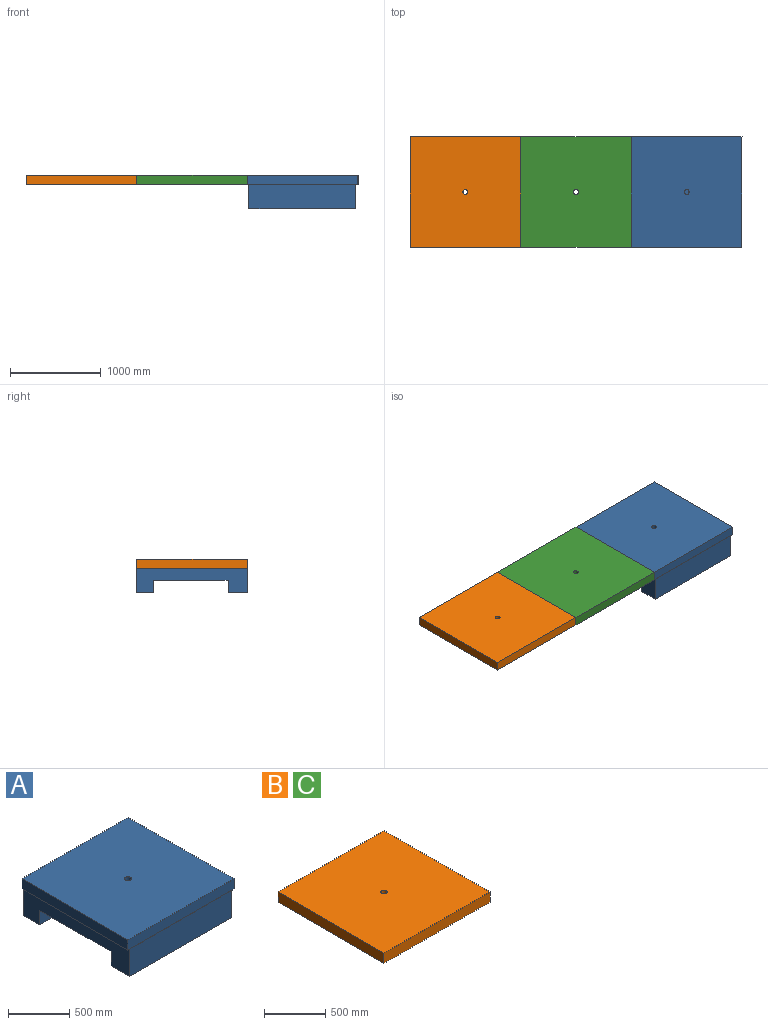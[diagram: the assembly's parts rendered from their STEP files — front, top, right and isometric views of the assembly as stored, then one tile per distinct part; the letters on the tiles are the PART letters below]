
ASSEMBLY  parts=3 mates=2
PART A: 17 faces, bbox 1219.2x1219.2x374 mm
  f0: plane 1219.2x1219.2mm, normal (0,0,-1), area 59318.6mm2, adj f1,f2,f3,f5,f7,f8,f9,f10
  f1: plane 1219.2x101.6mm, normal (0,-1,0), area 123870.7mm2, adj f0,f2,f5,f6
  f2: plane 1219.2x101.6mm, normal (1,0,0), area 123870.7mm2, adj f0,f1,f3,f6
  f3: plane 1219.2x101.6mm, normal (0,1,0), area 123870.7mm2, adj f0,f2,f5,f6
  f4: cylinder r=27.54mm len=101.6mm, axis (0,0,-1), area 17582mm2, adj f6,f16
  f5: plane 1219.2x101.6mm, normal (-1,0,0), area 123870.7mm2, adj f0,f1,f3,f6
  f6: plane 1219.2x1219.2mm, normal (0,0,1), area 1484065.6mm2, adj f1,f2,f3,f4,f5
  f7: plane 1216.15x272.36mm, normal (-1,0,0), area 214341.6mm2, adj f0,f9,f10,f11,f12,f13,f14,f15
  f8: plane 1216.15x272.36mm, normal (1,0,0), area 214341.6mm2, adj f0,f9,f10,f11,f12,f13,f14,f15
  f9: plane 1173.48x272.36mm, normal (0,-1,0), area 319607.7mm2, adj f0,f7,f8,f15
  f10: plane 1173.48x272.36mm, normal (0,1,0), area 319607.7mm2, adj f0,f7,f8,f11
  f11: plane 1173.48x187.56mm, normal (0,0,-1), area 220095.9mm2, adj f7,f8,f10,f12
  f12: plane 1173.48x142.9mm, normal (0,-1,0), area 167692.2mm2, adj f7,f8,f11,f13
  f13: plane 1173.48x817.96mm, normal (0,0,-1), area 959862.9mm2, adj f7,f8,f12,f14
  f14: plane 1173.48x142.9mm, normal (0,1,0), area 167692.2mm2, adj f7,f8,f13,f15
  f15: plane 1173.48x210.63mm, normal (0,0,-1), area 247171.2mm2, adj f7,f8,f9,f14
  f16: plane 55.08x55.08mm, normal (0,0,1), area 2383.1mm2, adj f4
PART B: 7 faces, bbox 1219.2x1219.2x101.6 mm
  f0: plane 1219.2x101.6mm, normal (0,-1,0), area 123870.7mm2, adj f1,f4,f5,f6
  f1: plane 1219.2x101.6mm, normal (1,0,0), area 123870.7mm2, adj f0,f2,f5,f6
  f2: plane 1219.2x101.6mm, normal (0,1,0), area 123870.7mm2, adj f1,f4,f5,f6
  f3: cylinder r=26.3mm len=101.6mm, axis (0,0,-1), area 16791mm2, adj f5,f6
  f4: plane 1219.2x101.6mm, normal (-1,0,0), area 123870.7mm2, adj f0,f2,f5,f6
  f5: plane 1219.2x1219.2mm, normal (0,0,1), area 1484275.2mm2, adj f0,f1,f2,f3,f4
  f6: plane 1219.2x1219.2mm, normal (0,0,-1), area 1484275.2mm2, adj f0,f1,f2,f3,f4
PART C: same geometry as B
PLACE A t=(-42.52,28.94,-4.42)mm
PLACE B t=(-2480.92,28.94,-4.42)mm
PLACE C t=(-1261.72,28.94,-4.42)mm
MATE planar C.f3 <-> A.f4  axis (0,0,1) through (-1261.72,28.94,97.18)mm
MATE planar B.f3 <-> A.f4  axis (0,0,1) through (-2480.92,28.94,97.18)mm
